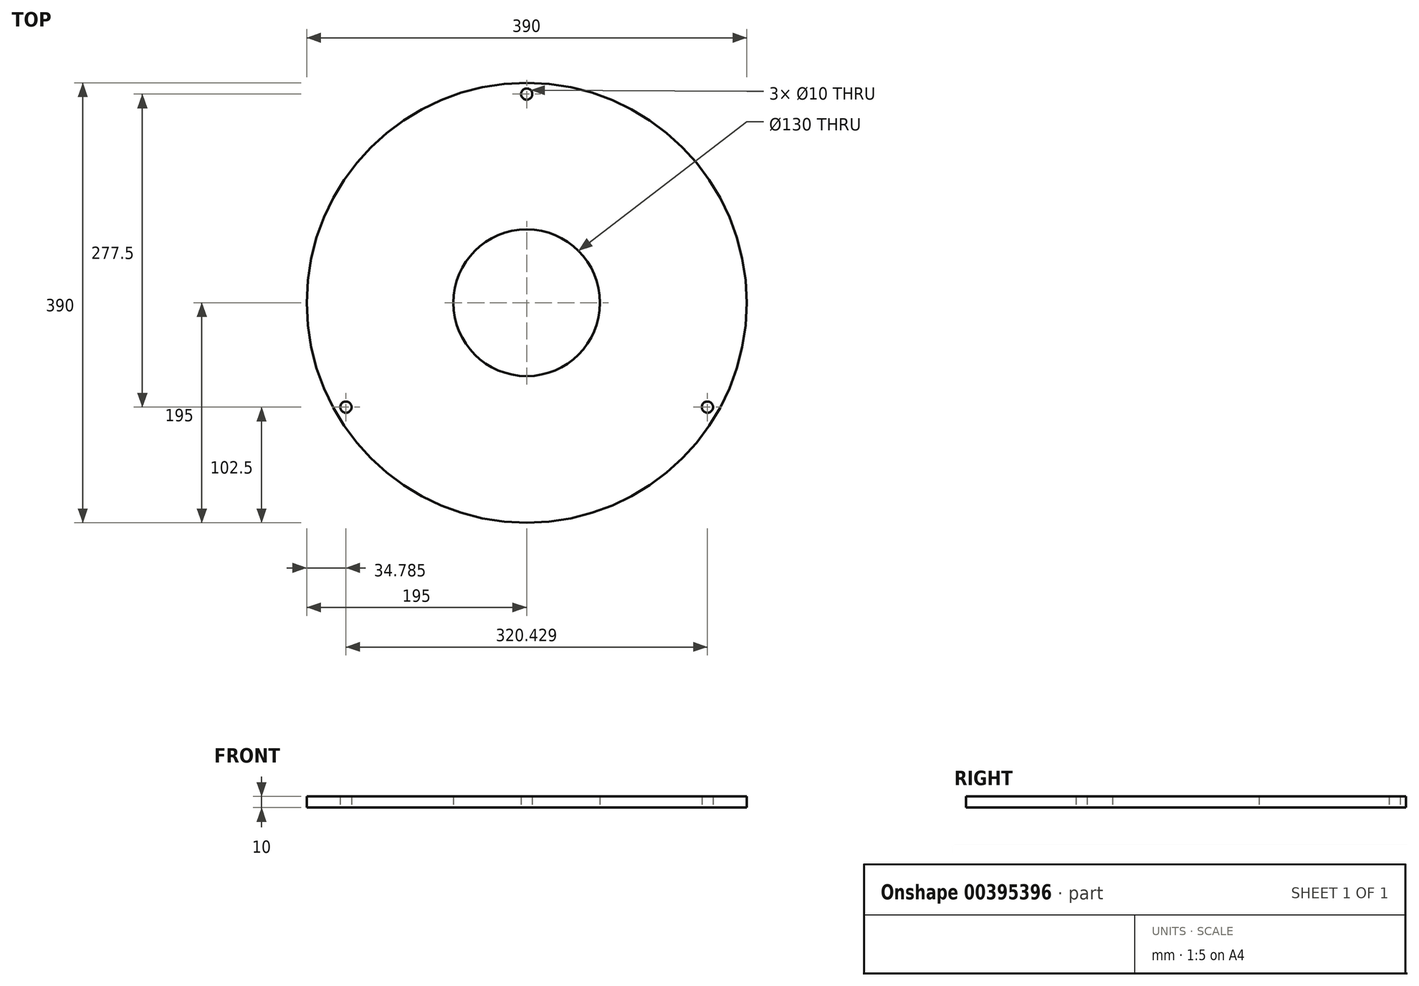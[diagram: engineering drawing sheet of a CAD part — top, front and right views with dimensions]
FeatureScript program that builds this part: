
annotation { "Feature Type Name" : "Feature", "Feature Type Description" : "" }
export const myFeature = defineFeature(function(context is Context, id is Id, definition is map)
    precondition{}
    {
        {
            assignVariable(context, id + "F0", {"name" : "hmodule", "anyValue" : 10});
        }
        {
            var Q0;
            Q0=qCreatedBy(makeId("Top.planeOp"),FACE);
            var sketch = newSketch(context, id + "F1", { "sketchPlane" : qUnion([Q0])});
            skCircle(sketch, "E0", {"center": v(0, 0) * mm, "radius": 65 * mm});
            skCircle(sketch, "E1", {"center": v(0, 0) * mm, "radius": 195 * mm});
            skCircle(sketch, "E2", {"center": v(0, 185) * mm, "radius": 5 * mm});
            skCircle(sketch, "E3.1.0", {"center": v(-160.21, -92.5) * mm, "radius": 5 * mm});
            skCircle(sketch, "E3.2.0", {"center": v(160.21, -92.5) * mm, "radius": 5 * mm});
            skSolve(sketch);
        }
        {
            var Q0;
            Q0=makeQuery(id+"F1.imprint","IMPRINT",FACE,{"disambiguationData":[TD([[makeQuery(id+"F1.imprint","IMPRINT",EDGE,{"derivedFrom":sQuery(id+"F1.wireOp",EDGE,"E0")}),-1.0]])]});
            extrude(context, id + "F2", {"entities" : qUnion([Q0]), "depth" : (getVariable(context, 'hmodule')) * mm});
        }
    });
